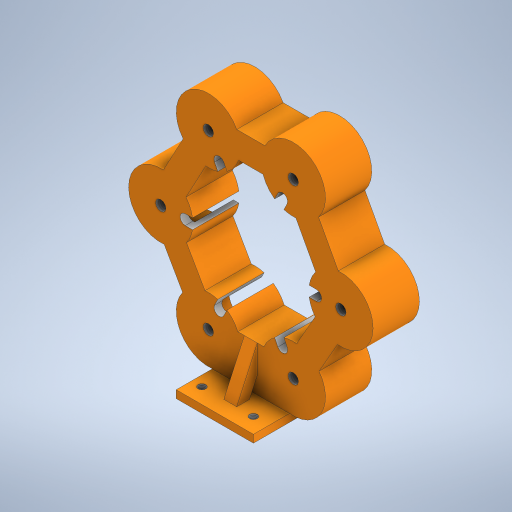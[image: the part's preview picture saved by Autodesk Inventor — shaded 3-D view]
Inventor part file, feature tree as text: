
AUTODESK INVENTOR PART (.ipt)
format: ipt  version: 2023 (Build 270158000, 158)  size: 628,224 bytes
history: native  units: in
note: dims shown in document units (in); Inventor stores cm internally (conversion verified against a paired STEP export)
features: thread x8, sketch x7, extrude x7, hole x2, rib x1
ambient origin geometry x8: Origin, YZ Plane, XZ Plane, XY Plane, X Axis, Y Axis, Z Axis, Center Point
bodies: Body1 (feature_tree)
feature tree (25):
  sketch  "Sketch1"  dims[d0=3.937in d16=1.1811in d17=0.9055in]
  extrude  "Extrusion7"  Depth=1.1811in
  extrude  "Extrusion8"  Depth=1.1811in
  extrude  "Extrusion9"  Depth=1.1811in
  extrude  "Extrusion10"  Depth=0.8661in
  extrude  "Extrusion11"  Depth=0.0591in
  extrude  "Extrusion12"  Depth=0.0591in
  sketch  "Sketch10"  dims[d32=0.0591in d33=3.937in]
  rib  "Rib1"
  thread  "Thread1"  [1 undecoded]
  thread  "Thread2"  [1 undecoded]
  thread  "Thread3"  [1 undecoded]
  thread  "Thread4"  [1 undecoded]
  thread  "Thread5"  [1 undecoded]
  thread  "Thread6"  [1 undecoded]
  extrude  "Extrusion14"  Depth=0.1181in
  sketch  "Sketch13"  dims[d43=0.2362in d45=0.8661in d46=5.5118in d83=0.8189in d84=0.8189in d85=0.8189in d87=0.9843in d88=0.9843in d89=0.9843in d90=0.9843in d91=0.9843in d92=0.9843in d93=0.7087in d94=0.0in d95=0.5906in d96=0.0in d99=0.1969in d100=0.1969in d101=0.1969in d102=0.1969in d103=0.1969in d104=0.1969in d105=0.1969in d106=0.1969in d107=0.1969in d108=0.1969in d109=0.3937in d110=0.7087in d111=0.0in d112=1.1811in d113=0.7087in d114=0.0in d115=1.1811in d116=1.2598in d117=0.1181in d118=0.0in d128=0.1575in d129=0.1575in d130=0.1575in d131=0.1575in d132=0.1575in d133=0.1575in d134=0.1181in d135=0.1575in d136=0.1181in d137=0.1575in d138=0.1181in d139=0.1575in d140=0.1181in d141=0.1575in d142=0.1181in d143=0.1575in d144=0.1181in d145=0.1575in d146=0.7087in d147=0.0in d148=0.315in d149=0.689in d150=0.0394in d151=0.1969in d152=0.0in d153=0.0in d154=0.0394in d155=0.0394in d159=0.1181in d160=0.0in d161=0.1181in d162=0.0in d163=0.1181in d164=0.0in d165=0.1181in d166=0.0in d167=0.1181in d168=0.0in d169=0.1181in d170=0.0in d176=0.1772in d177=0.3937in d178=0.0in d179=0.7874in d180=0.7874in d181=0.1181in d182=0.2362in d183=0.1575in d184=0.0787in d185=90.0deg d186=0.315in d187=0.8108in d188=0.1181in d189=0.2362in d190=0.1575in d191=0.0787in d192=90.0deg d193=0.315in d194=0.8108in d195=0.1181in d196=0.0in d197=0.1181in d198=0.0in]
  hole  "Hole3"  [1 undecoded]
  hole  "Hole4"  [1 undecoded]
  thread  "Thread9"  [1 undecoded]
  thread  "Thread10"  [1 undecoded]
  sketch  "Sketch6"  dims[d20=1.1811in d21=0.9055in d22=1.1811in d23=0.9055in]
  sketch  "Sketch7"  dims[d24=1.1811in d25=0.9055in d26=1.1811in d27=0.9055in]
  sketch  "Sketch9"  dims[d30=0.8661in d31=0.8661in]
  sketch  "Sketch12"  dims[d35=0.8661in d36=0.0591in d37=0.8661in d38=0.8189in d39=0.8189in d40=0.0591in d41=0.1575in d42=0.1575in]
note: 10 required parameter values undecoded (feature->parameter linkage not recoverable at this tier; creation-order binding heuristic only, values carry confidence <= 0.55)
